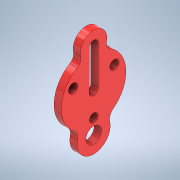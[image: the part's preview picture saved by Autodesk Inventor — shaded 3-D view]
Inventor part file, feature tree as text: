
AUTODESK INVENTOR PART (.ipt)
format: ipt  version: 2021 (Build 250183000, 183)  size: 146,432 bytes
history: native  units: in
note: dims shown in document units (in); Inventor stores cm internally (conversion verified against a paired STEP export)
features: extrude x1, sketch x1
ambient origin geometry x8: Origin, YZ Plane, XZ Plane, XY Plane, X Axis, Y Axis, Z Axis, Center Point
bodies: Solid1 (feature_tree)
feature tree (2):
  extrude  "Extrusion1"  Depth=1.4173in
  sketch  "Sketch1"  dims[d19=0.4921in d20=1.4173in d21=4.1732in d22=8.3465in d23=0.9843in d24=0.9843in d25=1.6929in d26=1.7717in d27=0.9055in d28=3.4646in d29=0.9843in d30=0.9843in d31=0.7874in d32=0.7874in d33=0.7874in d34=0.0in]
